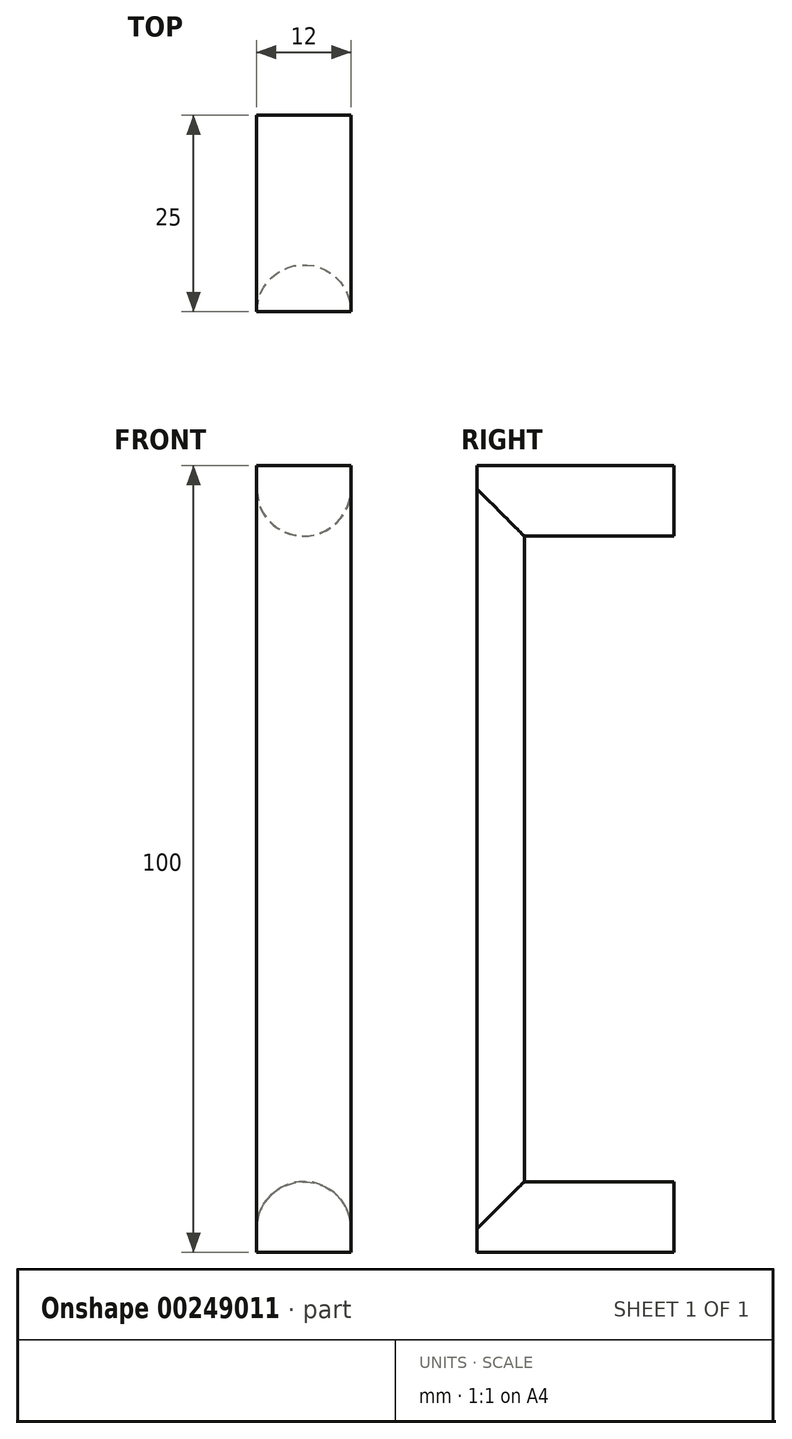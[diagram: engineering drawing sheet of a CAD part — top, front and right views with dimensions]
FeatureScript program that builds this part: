
annotation { "Feature Type Name" : "Feature", "Feature Type Description" : "" }
export const myFeature = defineFeature(function(context is Context, id is Id, definition is map)
    precondition{}
    {
        {
            var Q0;
            Q0=qCreatedBy(makeId("Right.planeOp"),FACE);
            var sketch = newSketch(context, id + "F0", { "sketchPlane" : qUnion([Q0])});
            skLineSegment(sketch, "E0.bottom", {"start": v(-25, 47) * mm, "end": v(0, 47) * mm});
            skLineSegment(sketch, "E0.top", {"start": v(-25, -47) * mm, "end": v(0, -47) * mm});
            skLineSegment(sketch, "E0.left", {"start": v(-25, 47) * mm, "end": v(-25, -47) * mm});
            skPoint(sketch, "E0.middle", {"position": v(0, 0) * mm});
            skSolve(sketch);
        }
        {
            var Q0;
            Q0=qCreatedBy(makeId("Front.planeOp"),FACE);
            var sketch = newSketch(context, id + "F1", { "sketchPlane" : qUnion([Q0])});
            skLineSegment(sketch, "E1", {"start": v(-6, 47) * mm, "end": v(6, 47) * mm});
            skArc(sketch, "E2", {"start": v(-6, 47) * mm, "mid": v(0, 41) * mm, "end": v(6, 47) * mm});
            skSolve(sketch);
        }
        {
            var Q0;
            Q0=makeQuery(id+"F1.imprint","IMPRINT",FACE,{"disambiguationData":[TD([[makeQuery(id+"F1.imprint","IMPRINT",EDGE,{"derivedFrom":sQuery(id+"F1.wireOp",EDGE,"E1")}),-1.0]])]});
            var Q1;
            Q1=sQuery(id+"F0.wireOp",EDGE,"E0.bottom");
            var Q2;
            Q2=sQuery(id+"F0.wireOp",EDGE,"E0.left");
            var Q3;
            Q3=sQuery(id+"F0.wireOp",EDGE,"E0.top");
            sweep(context, id + "F2", {"profiles" : qUnion([Q0]), "path" : qUnion([Q1, Q2, Q3])});
        }
        {
            var Q0;
            Q0=makeQuery(id+"F2.opSweep","SWEPT_FACE",FACE,{"disambiguationData":[OSD([sQuery(id+"F0.wireOp",EDGE,"E0.bottom"),sQuery(id+"F1.wireOp",EDGE,"E1")])]});
            extrude(context, id + "F3", {"entities" : qUnion([Q0]), "operationType" : NewBodyOperationType.ADD, "depth" : 3 * mm});
        }
        {
            var Q0;
            Q0=makeQuery(id+"F2.opSweep","SWEPT_FACE",FACE,{"disambiguationData":[OSD([sQuery(id+"F0.wireOp",EDGE,"E0.top"),sQuery(id+"F1.wireOp",EDGE,"E1")])]});
            extrude(context, id + "F4", {"entities" : qUnion([Q0]), "operationType" : NewBodyOperationType.ADD, "depth" : 3 * mm});
        }
    });
